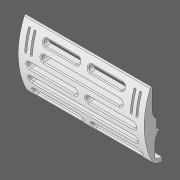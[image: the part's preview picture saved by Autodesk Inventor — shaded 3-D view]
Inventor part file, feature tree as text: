
AUTODESK INVENTOR PART (.ipt)
format: ipt  version: 2020 (Build 240168000, 168)  size: 624,640 bytes
history: native  units: in
note: dims shown in document units (in); Inventor stores cm internally (conversion verified against a paired STEP export)
features: extrude x3, fillet x2, other x2, sketch x2
ambient origin geometry x8: Origin, YZ Plane, XZ Plane, XY Plane, X Axis, Y Axis, Z Axis, Center Point
bodies: Solid1 (feature_tree)
feature tree (9):
  extrude  "Slots"  Depth=0.0591in
  extrude  "Extrusion3"  Depth=0.0118in
  fillet  "Fillet2"  Radius=0.0118in
  extrude  "Extrusion4"  Depth=0.1181in
  fillet  "Fillet3"  Radius=0.2362in
  other  "Profile"
  other  "Slot Sketch"
  sketch  "Sketch3"  dims[d0=7.0866in d1=0.0in d3=0.0591in]
  sketch  "Sketch4"  dims[d5=0.5906in d14=0.0118in d15=0.0118in d16=0.1181in d17=0.2362in d18=0.1181in d19=0.3056in d20=0.2362in d21=0.5978in d22=0.0in d26=0.0118in d27=0.0118in d28=0.1181in d29=0.2362in d30=0.1181in d31=0.0079in d35=6.6142in d36=0.0118in d37=0.0118in d38=0.1181in d39=0.2362in d40=0.1181in d41=0.0079in d45=3.3071in d48=3.5433in d50=0.7874in d51=1.1811in d52=0.1181in d53=0.4724in d54=0.0in d55=0.0in d56=0.1969in d57=0.1969in d58=0.0591in d59=0.1575in d62=4.252in d71=0.0in d72=0.0in d83=3.5433in d85=0.2953in d86=0.6299in d87=0.3937in d88=0.3937in d89=0.3937in d92=0.6299in d93=0.0591in d95=0.3937in d96=0.6299in d97=0.3937in d98=4.252in d99=0.3937in d100=4.3307in d114=0.7874in d115=0.3056in d122=0.2362in d124=0.2362in d127=0.1181in d129=0.7874in d130=1.634in d131=0.4724in d133=0.7874in d134=0.2362in d135=0.1181in d136=0.3937in]
